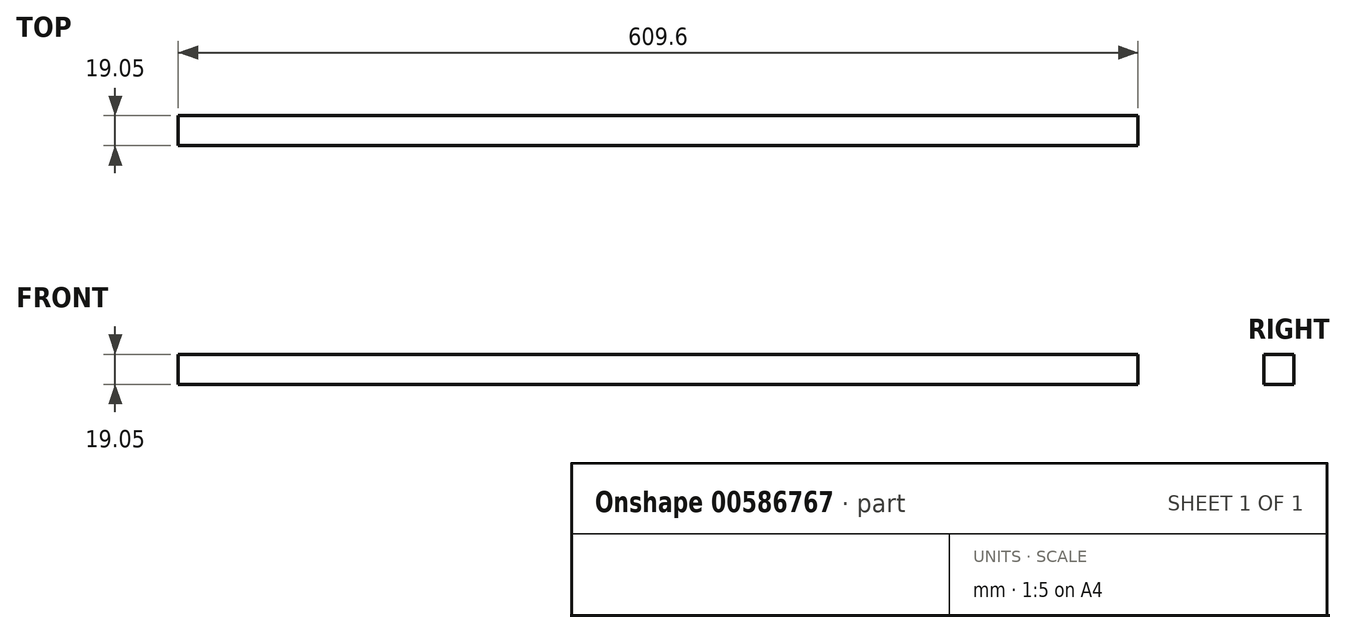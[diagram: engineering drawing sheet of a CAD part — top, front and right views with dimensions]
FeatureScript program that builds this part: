
annotation { "Feature Type Name" : "Feature", "Feature Type Description" : "" }
export const myFeature = defineFeature(function(context is Context, id is Id, definition is map)
    precondition{}
    {
        {
            var Q0;
            Q0=qCreatedBy(makeId("Top.planeOp"),FACE);
            var sketch = newSketch(context, id + "F0", { "sketchPlane" : qUnion([Q0])});
            skLineSegment(sketch, "E0.bottom", {"start": v(-62.2, 4.1) * mm, "end": v(547.4, 4.1) * mm});
            skLineSegment(sketch, "E0.top", {"start": v(-62.2, -14.96) * mm, "end": v(547.4, -14.96) * mm});
            skLineSegment(sketch, "E0.left", {"start": v(-62.2, 4.1) * mm, "end": v(-62.2, -14.96) * mm});
            skLineSegment(sketch, "E0.right", {"start": v(547.4, 4.1) * mm, "end": v(547.4, -14.96) * mm});
            skSolve(sketch);
        }
        {
            var Q0;
            Q0 = qSketchRegion(id + "F0", true);
            extrude(context, id + "F1", {"entities" : qUnion([Q0]), "depth" : 19.05 * mm, "offsetDistance" : 25.4 * mm});
        }
    });
